# Revit family: AP-5122m
name_source: partatom
category: Communication Devices
revit_build: Autodesk Revit Architecture 2012 (Build: 20110309_2315(x64)
units: mm (PartAtom-declared; Revit-internal decimal feet)

## types (1)
- AP-5122m
    Coverage Horizontal = 90.00°
    Coverage Vertical = 90.00°
    Default Elevation = 0 mm
    Depth = 292 mm
    Description = 12-inch, Two-way Multipurpose Enclosure with 90-degree Axisymmetric Coverage
12-inch, Two-way Trapezoidal Enclosure with 90-degree Axisymmetric Coverage
    Front Curve Raidus = 80 mm
    Grill Apex to Apex = 296 mm
    Grill Height = 630 mm
    Grill Rear Offset from Front = 42 mm
    Height = 660 mm
    Impedance = 8
    Manufacturer = QSC Audio Products, LLC
    Manufacturer URL = www.qscaudio.com
    Model = AP-5122m
    Power Handling = 550
    Product Documentation Link = http://qscmarketing.com
    Product Page URL = http://www.qsc.com
    Rear Face Width = 49 mm
    Regulatory Compliance = RoHS
    SPL Max = 128
    Sensitivity = 95
    Taper Offset from Front = 147 mm
    URL = http://www.qsc.com
    Weight Dimensional (kg) = 33
    Weight Dimensional (lb) = 72
    Weight Product (kg) = 29.5
    Weight Product (lb) = 65
    Width = 381 mm

## geometry (parser evidence)
native form markers: Sweep x1
no freeform markers — native parametric forms only
